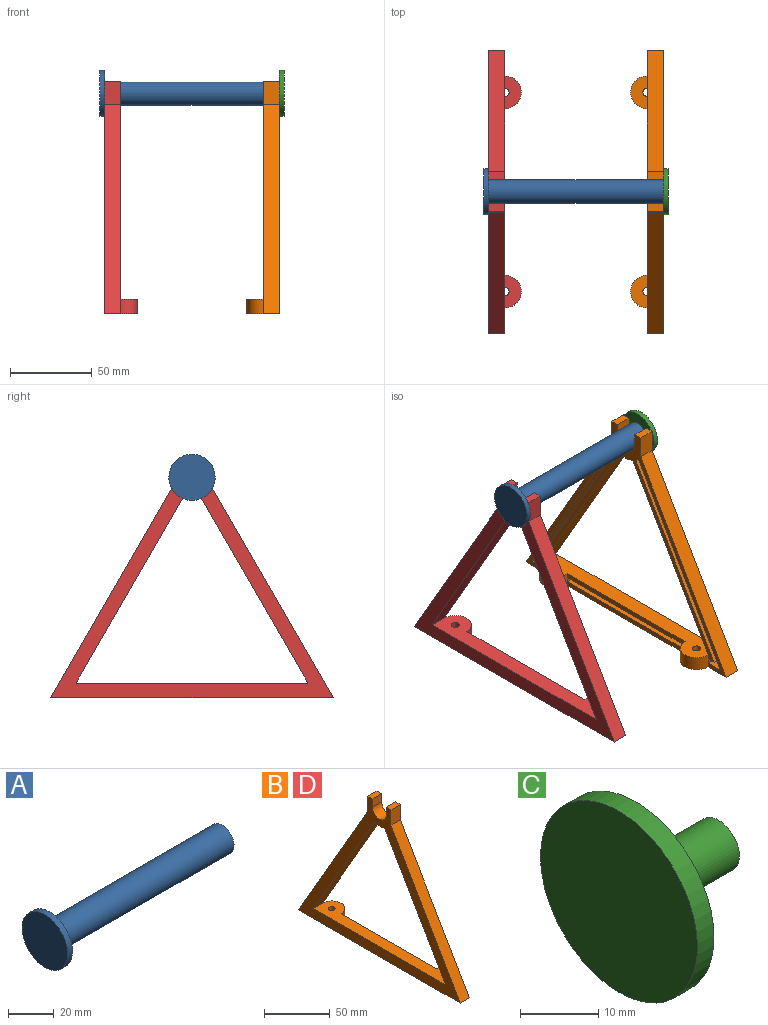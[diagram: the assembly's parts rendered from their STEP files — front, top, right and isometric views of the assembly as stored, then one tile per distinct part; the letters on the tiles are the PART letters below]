
ASSEMBLY  parts=4 mates=4
PART A: 7 faces, bbox 110x28.3x28.3 mm
  f0: cylinder r=14.16mm len=28.32mm, axis (-1,0,0), area 266.9mm2, adj f1,f2
  f1: plane 28.32x28.32mm, normal (1,0,0), area 464.7mm2, adj f0,f4
  f2: plane 28.32x28.32mm, normal (-1,0,0), area 629.8mm2, adj f0
  f3: cylinder r=4mm len=20mm, axis (-1,0,0), area 502.7mm2, adj f5,f6
  f4: cylinder r=7.25mm len=107mm, axis (-1,0,0), area 4874.2mm2, adj f1,f5
  f5: plane 14.5x14.5mm, normal (1,0,0), area 114.9mm2, adj f3,f4
  f6: plane 8x8mm, normal (1,0,0), area 50.3mm2, adj f3
PART B: 41 faces, bbox 20x173.2x142.5 mm
  f0: plane 142.03x20mm, normal (0,0,1), area 1695.2mm2, adj f4,f9,f27,f29,f35,f36,f39,f40
  f1: plane 10.39x5mm, normal (0,0,1), area 52mm2, adj f5,f12,f31,f37
  f2: plane 5.2x5mm, normal (0,0,-1), area 26mm2, adj f5,f26,f31,f37
  f3: plane 102.03x3mm, normal (1,0,0), area 306.1mm2, adj f11,f30,f36,f39
  f4: plane 102.03x3mm, normal (1,0,0), area 306.1mm2, adj f0,f25,f36,f39
  f5: plane 122.62x73.07mm, normal (1,0,0), area 439.2mm2, adj f1,f2,f12,f14,f26,f37
  f6: plane 10.39x5mm, normal (0,0,1), area 52mm2, adj f8,f10,f31,f33
  f7: plane 5.2x5mm, normal (0,0,-1), area 26mm2, adj f8,f24,f31,f33
  f8: plane 122.62x73.07mm, normal (1,0,0), area 439.2mm2, adj f6,f7,f10,f13,f24,f33
  f9: plane 173.21x142.5mm, normal (-1,0,0), area 4204.4mm2, adj f0,f15,f16,f17,f18,f19,f20,f21
  f10: plane 122.62x70.8mm, normal (0,0.87,-0.5), area 708mm2, adj f6,f8,f13,f31
  f11: plane 102.03x5mm, normal (0,0,1), area 510.1mm2, adj f3,f32,f34,f38
  f12: plane 122.62x70.8mm, normal (0,-0.87,-0.5), area 708mm2, adj f1,f5,f14,f31
  f13: cylinder r=14.16mm len=5mm, axis (-1,0,0), area 15.4mm2, adj f8,f10,f24,f31
  f14: cylinder r=14.16mm len=5mm, axis (-1,0,0), area 15.4mm2, adj f5,f12,f26,f31
  f15: plane 128.35x74.1mm, normal (0,0.87,0.5), area 1482.1mm2, adj f9,f16,f30,f31
  f16: plane 14.15x10mm, normal (0,1,0), area 141.5mm2, adj f9,f15,f17,f31
  f17: plane 10x5mm, normal (0,0,1), area 50mm2, adj f9,f16,f18,f31
  f18: plane 10x7.5mm, normal (0,-1,0), area 75mm2, adj f9,f17,f19,f31
  f19: cylinder r=7.5mm len=15mm, axis (-1,0,0), area 235.6mm2, adj f9,f18,f20,f31
  f20: plane 10x7.5mm, normal (0,1,0), area 75mm2, adj f9,f19,f21,f31
  f21: plane 10x5mm, normal (0,0,1), area 50mm2, adj f9,f20,f22,f31
  f22: plane 14.15x10mm, normal (0,-1,0), area 141.5mm2, adj f9,f21,f23,f31
  f23: plane 128.35x74.1mm, normal (0,-0.87,0.5), area 1482.1mm2, adj f9,f22,f30,f31
  f24: plane 117.56x67.87mm, normal (0,-0.87,0.5), area 678.7mm2, adj f7,f8,f13,f31
  f25: plane 102.03x5mm, normal (0,0,-1), area 510.1mm2, adj f4,f32,f34,f38
  f26: plane 117.56x67.87mm, normal (0,0.87,0.5), area 678.7mm2, adj f2,f5,f14,f31
  f27: plane 113.06x65.27mm, normal (0,0.87,-0.5), area 1305.5mm2, adj f0,f9,f28,f31
  f28: cylinder r=14.16mm len=11.48mm, axis (-1,0,0), area 118.2mm2, adj f9,f27,f29,f31
  f29: plane 113.06x65.27mm, normal (0,-0.87,-0.5), area 1305.5mm2, adj f0,f9,f28,f31
  f30: plane 173.21x20mm, normal (0,0,-1), area 2006.9mm2, adj f3,f9,f15,f23,f31,f35,f36,f39
  f31: plane 173.21x142.5mm, normal (1,0,0), area 2047.7mm2, adj f1,f2,f6,f7,f10,f12,f13,f14
  f32: plane 102.03x3mm, normal (1,0,0), area 306.1mm2, adj f11,f25,f34,f38
  f33: plane 5x3mm, normal (0,-1,0), area 15mm2, adj f6,f7,f8,f36
  f34: plane 5x3mm, normal (0,1,0), area 15mm2, adj f11,f25,f32,f36
  f35: cylinder r=2.5mm len=9mm, axis (0,0,-1), area 141.4mm2, adj f0,f30
  f36: cylinder r=10mm len=20mm, axis (0,0,-1), area 282.7mm2, adj f0,f3,f4,f30,f31,f33,f34
  f37: plane 5x3mm, normal (0,1,0), area 15mm2, adj f1,f2,f5,f39
  f38: plane 5x3mm, normal (0,-1,0), area 15mm2, adj f11,f25,f32,f39
  f39: cylinder r=10mm len=20mm, axis (0,0,-1), area 282.7mm2, adj f0,f3,f4,f30,f31,f37,f38
  f40: cylinder r=2.5mm len=9mm, axis (0,0,-1), area 141.4mm2, adj f0,f30
PART C: 5 faces, bbox 18x28.3x28.3 mm
  f0: cylinder r=14.16mm len=28.32mm, axis (-1,0,0), area 266.9mm2, adj f1,f2
  f1: plane 28.32x28.32mm, normal (1,0,0), area 585.7mm2, adj f0,f3
  f2: plane 28.32x28.32mm, normal (-1,0,0), area 629.8mm2, adj f0
  f3: cylinder r=3.75mm len=15mm, axis (-1,0,0), area 353.4mm2, adj f1,f4
  f4: plane 7.5x7.5mm, normal (1,0,0), area 44.2mm2, adj f3
PART D: same geometry as B
PLACE A t=(-3,166.6,135)mm
PLACE B rot(axis=(0,0,1),180deg) t=(107,173.21,0)mm
PLACE C rot(axis=(0,0,1),180deg) t=(110,46.6,135)mm
PLACE D at identity
MATE planar B.f39 <-> D.f35  axis (0,0,-1) through (97,25.59,0)mm
MATE revolute D.f13 <-> A.f4  axis (-1,0,0) through (0,86.6,135)mm
MATE revolute C.f0 <-> B.f13  axis (-1,0,0) through (107,86.6,135)mm
MATE fastened C.f3 <-> A.f3  axis (-1,0,0) through (107,86.6,135)mm
